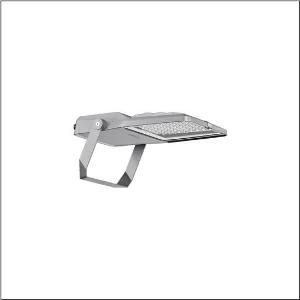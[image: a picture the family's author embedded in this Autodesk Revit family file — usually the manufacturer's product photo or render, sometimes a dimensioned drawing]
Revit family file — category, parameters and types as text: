
# Revit family: floodlight_fl_21_iq_mini___pl61_5xa7772d3c1a_e68f
name_source: partatom
category: Lighting Fixtures
units: mm (PartAtom-declared; Revit-internal decimal feet)

## family parameters
Cut with Voids When Loaded = No
Host = Face
Light Source = No
Part Type = Normal
Room Calculation Point = No
Round Connector Dimension = Use Diameter
Shared = No

## types (1)
- --- (1 x LED, 15060 lm, 143 W, 3000K)
    Apparent Load = 143 VA
    CIE Flux Codes = 33 65 98 100 100
    Color Rendering = 80
    Color Temperature = 3000K
    Default Elevation = 1800 mm
    Description = Floodlight FL 21 iQ mini, floodlight, primary light control with lens, of PMMA, primary optical cover: protective disc, of toughened safety glass, transparent, light distribution: PL61, light emission: direct distribution, installation type: surface-mounted, LED, High Power LED, rated luminous flux: 15.060lm, luminous efficacy: 105lm/W, light colour: 830, colour temperature: 3000K, control: Street-Remote, Auto-Match, Temp-Guard, Night-Set, Smart-Wire, Desk-Remote (wireless, voltage-free reading and setting of iQ features in the workshop via application-optimized NFC function/RFID function), optimised constant luminous flux control (CLO 2.0), with terminal, 6-pole, mains connection: 220..240V, AC, 50/60Hz, start of lifetime: 143W, end of service life: 152W, reduction: 61W, luminaire housing, of diecast aluminium, powder-coated, Siteco® metallic grey (DB 702S), corrosivity category C5 mid according to DIN EN ISO 12944, sealing non-destructively replaceable, mounting bracket, of steel, galvanised, powder-coated, Siteco® metallic grey (DB 702S), protection rating (complete): IP66, insulation class (complete): insulation class II (safety insulation), certification: CE, ENEC, VDE, protection symbol: D, impact resistance: IK08, permissible operating ambient temperature: -40..+40°C, permissible operating ambient temperature for outdoor applications: -40..+50°C, standard: DIN EN 12944, LABS conformity tested according to VDMA 24364:2018-05, packaging unit: 1 piece

Light Distribution: PL61
    Height = 70 mm
    Lamp = 1 x LED
    Lamp Light Flux = 15060 lm
    Lamp Power = 143 W
    Lamp count = 1
    Length = 485 mm
    Luminous efficacy = 105 lm/W
    Manufacturer = Siteco
    ModVariant = No
    Model = 5XA7772D3C1A
    Number of Poles = 1
    OnlyDefault = Yes
    Power Factor = 1
    Product Name = Floodlight FL 21 iQ mini | PL61
    Product group = floodlight | pylon annexe
    ProductGroupID = 6200
    Protection Class = Protection class II
    Protection Degree = IP 66
    RLX_Detail_Level = 1
    RLX_Emergency_Light_Flux = 0 lm
    RLX_Emergency_Type = 0
    RLX_Emergency_Type_DB = No
    RlxData = <blob elided: 96433 chars, md5=07273333>
    Socket = socket
    Standby Power = 0 W
    System Light Flux = 15060 lm
    System Power = 143 W
    Type Comments = factory setting: luminous flux: 100 % | dim-lin: 254 | 730 mA
    Type Image = l_1006845.jpg
    URL = http://relux.com
    VarID = @adj_105489
    Voltage = 0 V
    Weight = 0.00 kg
    Width = 337 mm

## geometry (parser evidence)
native form markers: Blend x4, Sweep x11
no freeform markers — native parametric forms only
